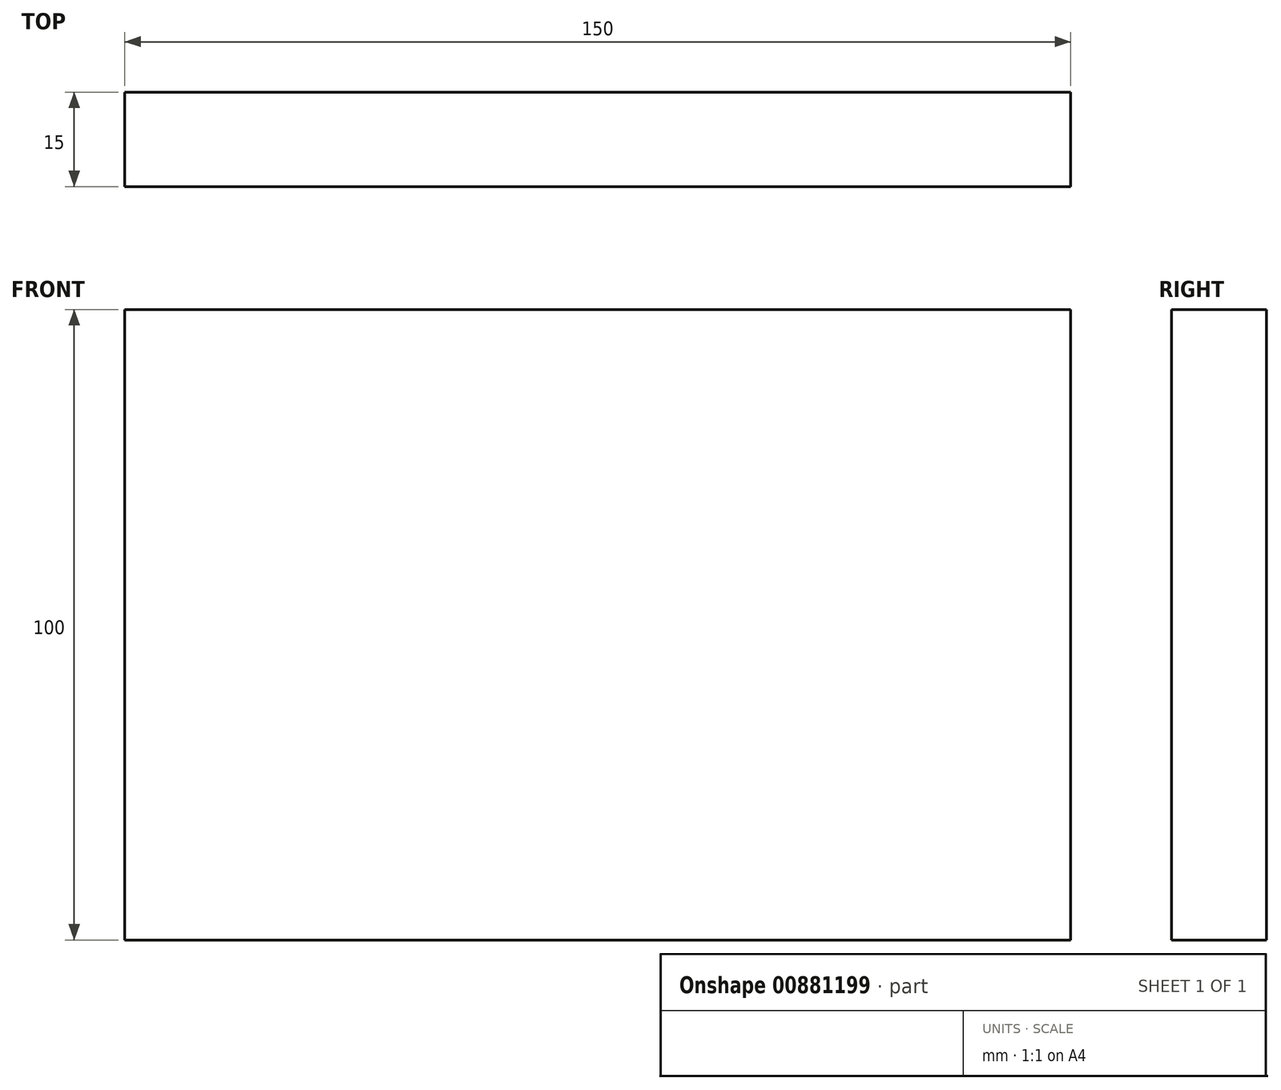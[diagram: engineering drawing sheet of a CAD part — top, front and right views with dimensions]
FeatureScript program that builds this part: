
annotation { "Feature Type Name" : "Feature", "Feature Type Description" : "" }
export const myFeature = defineFeature(function(context is Context, id is Id, definition is map)
    precondition{}
    {
        {
            var Q0;
            Q0=qCreatedBy(makeId("Front.planeOp"),FACE);
            var sketch = newSketch(context, id + "F0", { "sketchPlane" : qUnion([Q0])});
            skLineSegment(sketch, "E0.bottom", {"start": v(75, 50) * mm, "end": v(-75, 50) * mm});
            skLineSegment(sketch, "E0.top", {"start": v(75, -50) * mm, "end": v(-75, -50) * mm});
            skLineSegment(sketch, "E0.left", {"start": v(75, 50) * mm, "end": v(75, -50) * mm});
            skLineSegment(sketch, "E0.right", {"start": v(-75, 50) * mm, "end": v(-75, -50) * mm});
            skPoint(sketch, "E0.middle", {"position": v(0, 0) * mm});
            skSolve(sketch);
        }
        {
            var Q0;
            Q0 = qSketchRegion(id + "F0", true);
            extrude(context, id + "F1", {"entities" : qUnion([Q0]), "depth" : 15 * mm, "offsetDistance" : 25 * mm});
        }
    });
